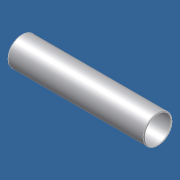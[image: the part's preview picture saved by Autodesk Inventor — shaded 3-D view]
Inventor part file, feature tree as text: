
AUTODESK INVENTOR PART (.ipt)
format: ipt  version: unknown  size: 208,384 bytes
history: native  units: in
note: dims shown in document units (in); Inventor stores cm internally (conversion verified against a paired STEP export)
features: other x42, revolve x1, sketch x1
ambient origin geometry x8: Origin, YZ Plane, XZ Plane, XY Plane, X Axis, Y Axis, Z Axis, Center Point
feature tree (44):
  revolve  "Revolution1"  [1 undecoded]
  other  "cp1_XY"
  other  "cp1_YZ"
  other  "cp1_ZX"
  other  "cp1_X"
  other  "cp1_Y"
  other  "cp1_Z"
  other  "cp1_Center"
  other  "cp2_XY"
  other  "cp2_YZ"
  other  "cp2_ZX"
  other  "cp2_X"
  other  "cp2_Y"
  other  "cp2_Z"
  other  "cp2_Center"
  other  "cp3_XY"
  other  "cp3_YZ"
  other  "cp3_ZX"
  other  "cp3_X"
  other  "cp3_Y"
  other  "cp3_Z"
  other  "cp3_Center"
  other  "cp4_XY"
  other  "cp4_YZ"
  other  "cp4_ZX"
  other  "cp4_X"
  other  "cp4_Y"
  other  "cp4_Z"
  other  "cp4_Center"
  other  "tube_front_XY"
  other  "tube_front_YZ"
  other  "tube_front_ZX"
  other  "tube_front_X"
  other  "tube_front_Y"
  other  "tube_front_Z"
  other  "tube_front_Center"
  other  "tube_rear_XY"
  other  "tube_rear_YZ"
  other  "tube_rear_ZX"
  other  "tube_rear_X"
  other  "tube_rear_Y"
  other  "tube_rear_Z"
  other  "tube_rear_Center"
  sketch  "Sketch_1"  dims[d0=360.0deg]
note: 1 required parameter value undecoded (feature->parameter linkage not recoverable at this tier; creation-order binding heuristic only, values carry confidence <= 0.55)
